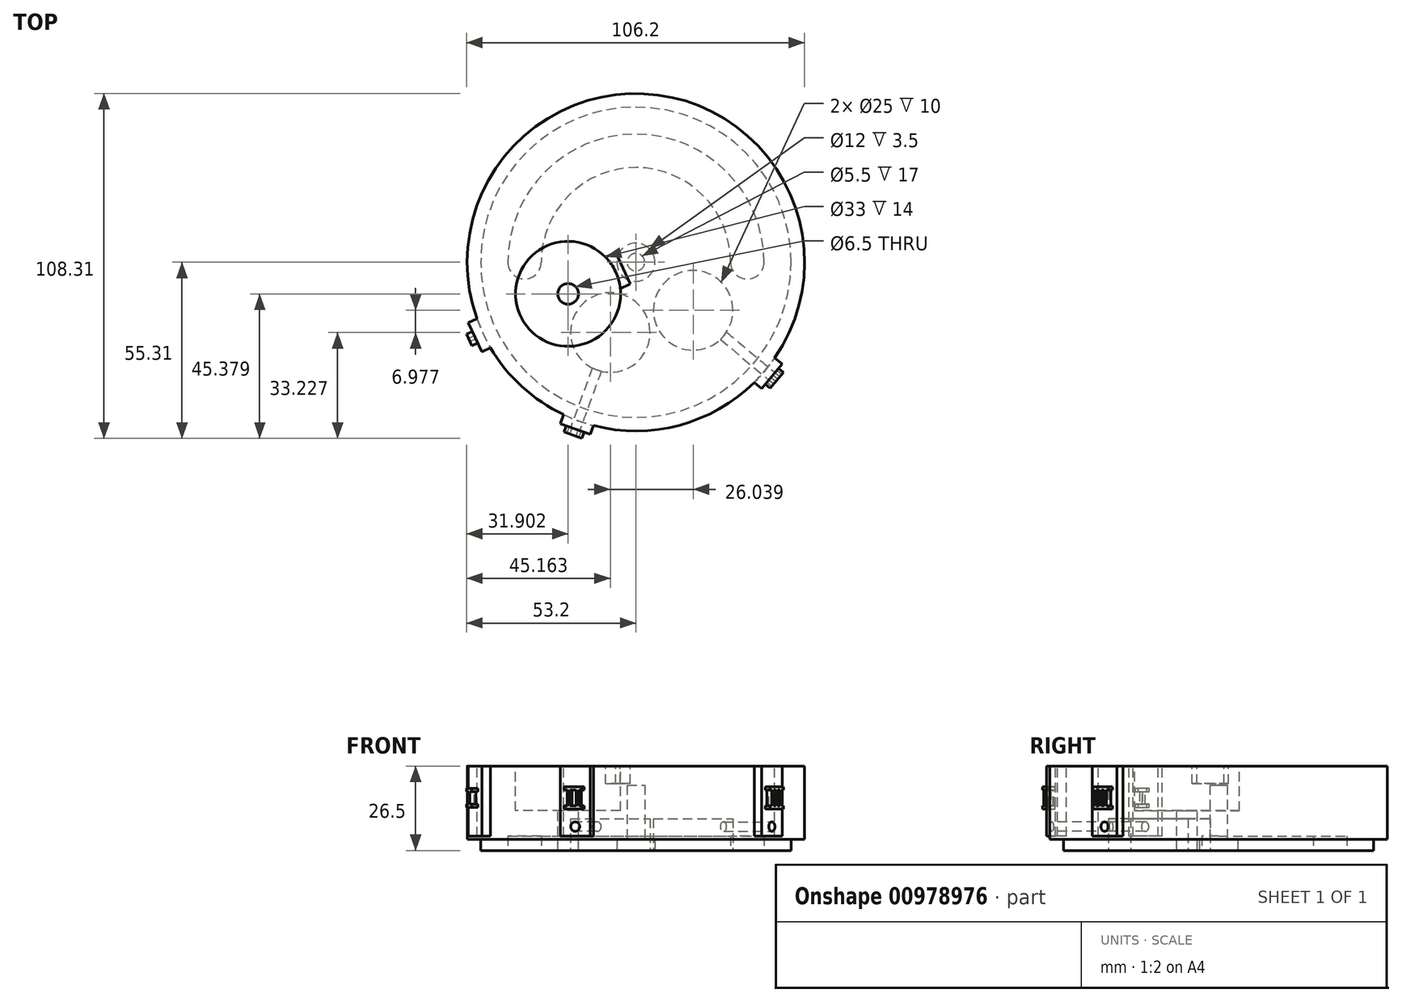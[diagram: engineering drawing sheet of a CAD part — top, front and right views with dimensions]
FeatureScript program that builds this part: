
annotation { "Feature Type Name" : "Feature", "Feature Type Description" : "" }
export const myFeature = defineFeature(function(context is Context, id is Id, definition is map)
    precondition{}
    {
        {
            var Q0;
            Q0=qCreatedBy(makeId("Top.planeOp"),FACE);
            var sketch = newSketch(context, id + "F0", { "sketchPlane" : qUnion([Q0])});
            skCircle(sketch, "E0", {"center": v(0, 0) * mm, "radius": 53 * mm});
            skSolve(sketch);
        }
        {
            var Q0;
            Q0=makeQuery(id+"F0.imprint","IMPRINT",FACE,{"disambiguationData":[TD([[makeQuery(id+"F0.imprint","IMPRINT",EDGE,{"derivedFrom":sQuery(id+"F0.wireOp",EDGE,"E0")}),1.0]])]});
            extrude(context, id + "F1", {"entities" : qUnion([Q0]), "depth" : 26.5 * mm, "offsetDistance" : 25 * mm});
        }
        {
            var Q0;
            Q0=makeQuery(id+"F1.opExtrude","CAP_FACE",FACE,{"disambiguationData":[OSD([sQuery(id+"F0.wireOp",EDGE,"E0")])],"isStart":true});
            var sketch = newSketch(context, id + "F2", { "sketchPlane" : qUnion([Q0])});
            skCircle(sketch, "E1", {"center": v(0, 0) * mm, "radius": 6 * mm});
            skCircle(sketch, "E2", {"center": v(0, 0) * mm, "radius": 48.75 * mm});
            skCircle(sketch, "E3", {"center": v(-35, 0) * mm, "radius": 5.25 * mm});
            skCircle(sketch, "E4", {"center": v(35, 0) * mm, "radius": 5.25 * mm});
            skCircle(sketch, "E5", {"center": v(0, 0) * mm, "radius": 29.75 * mm});
            skCircle(sketch, "E6", {"center": v(0, 0) * mm, "radius": 40.25 * mm});
            skCircle(sketch, "E7", {"center": v(-8.04, 22.08) * mm, "radius": 12.5 * mm});
            skCircle(sketch, "E8", {"center": v(18, 15.1) * mm, "radius": 12.5 * mm});
            skLineSegment(sketch, "E9", {"start": v(18, 15.1) * mm, "end": v(0, 0) * mm});
            skLineSegment(sketch, "E10", {"start": v(0, 0) * mm, "end": v(0, 10.25) * mm});
            skSolve(sketch);
        }
        {
            var Q0;
            Q0=makeQuery(id+"F2.imprint","IMPRINT",FACE,{"disambiguationData":[TD([[makeQuery(id+"F2.imprint","IMPRINT",EDGE,{"derivedFrom":sQuery(id+"F2.wireOp",EDGE,"E1")}),1.0]])]});
            var Q1;
            Q1=makeQuery(id+"F2.imprint","IMPRINT",FACE,{"disambiguationData":[TD([[makeQuery(id+"F2.imprint","IMPRINT",EDGE,{"derivedFrom":sQuery(id+"F2.wireOp",EDGE,"E2")}),-1.0]])]});
            extrude(context, id + "F3", {"entities" : qUnion([Q0, Q1]), "operationType" : NewBodyOperationType.REMOVE, "oppositeDirection" : true, "depth" : 3.5 * mm, "offsetDistance" : 25 * mm});
        }
        {
            var Q0;
            Q0=makeQuery(id+"F3.boolean.opBoolean","COPY",FACE,{"derivedFrom":makeQuery(id+"F3.opExtrude","CAP_FACE",FACE,{"disambiguationData":[OSD([sQuery(id+"F2.wireOp",EDGE,"E1")])],"isStart":false})});
            var sketch = newSketch(context, id + "F4", { "sketchPlane" : qUnion([Q0])});
            skCircle(sketch, "E11", {"center": v(0, 0) * mm, "radius": 2.75 * mm});
            skSolve(sketch);
        }
        {
            var Q0;
            Q0=makeQuery(id+"F4.imprint","IMPRINT",FACE,{"disambiguationData":[TD([[makeQuery(id+"F4.imprint","IMPRINT",EDGE,{"derivedFrom":sQuery(id+"F4.wireOp",EDGE,"E11")}),1.0]])]});
            extrude(context, id + "F5", {"entities" : qUnion([Q0]), "operationType" : NewBodyOperationType.REMOVE, "oppositeDirection" : true, "depth" : 17 * mm, "offsetDistance" : 25 * mm});
        }
        {
            var Q0;
            {var subQ0=sQuery(id+"F2.wireOp",EDGE,"E3");var subQ1=makeQuery(id+"F2.imprint","INTERSECT",VERTEX,{"derivedFrom":[subQ0,sQuery(id+"F2.wireOp",EDGE,"E5")]});Q0=makeQuery(id+"F2.imprint","IMPRINT",FACE,{"disambiguationData":[TD([[makeQuery(id+"F2.imprint","IMPRINT",EDGE,{"disambiguationData":[TD([[subQ1,-1.0]])],"derivedFrom":subQ0}),1.0]])]});}
            var Q1;
            {var subQ0=sQuery(id+"F2.wireOp",EDGE,"E5");var subQ1=sQuery(id+"F2.wireOp",EDGE,"E3");var subQ2=makeQuery(id+"F2.imprint","INTERSECT",VERTEX,{"derivedFrom":[subQ1,subQ0]});Q1=makeQuery(id+"F2.imprint","IMPRINT",FACE,{"disambiguationData":[TD([[makeQuery(id+"F2.imprint","IMPRINT",EDGE,{"disambiguationData":[TD([[subQ2,1.0]])],"derivedFrom":subQ1}),-1.0]])]});}
            var Q2;
            {var subQ0=sQuery(id+"F2.wireOp",EDGE,"E4");var subQ1=makeQuery(id+"F2.imprint","INTERSECT",VERTEX,{"derivedFrom":[subQ0,sQuery(id+"F2.wireOp",EDGE,"E5")]});Q2=makeQuery(id+"F2.imprint","IMPRINT",FACE,{"disambiguationData":[TD([[makeQuery(id+"F2.imprint","IMPRINT",EDGE,{"disambiguationData":[TD([[subQ1,1.0]])],"derivedFrom":subQ0}),1.0]])]});}
            extrude(context, id + "F6", {"entities" : qUnion([Q0, Q1, Q2]), "operationType" : NewBodyOperationType.REMOVE, "oppositeDirection" : true, "depth" : 4.5 * mm, "offsetDistance" : 25 * mm});
        }
        {
            var Q0;
            Q0=makeQuery(id+"F1.opExtrude","CAP_FACE",FACE,{"disambiguationData":[OSD([sQuery(id+"F0.wireOp",EDGE,"E0")])],"isStart":false});
            var sketch = newSketch(context, id + "F7", { "sketchPlane" : qUnion([Q0])});
            skCircle(sketch, "E12", {"center": v(-21.3, -9.93) * mm, "radius": 16.5 * mm});
            skLineSegment(sketch, "E13", {"start": v(-21.3, -9.93) * mm, "end": v(0, 0) * mm});
            skLineSegment(sketch, "E14", {"start": v(0, 0) * mm, "end": v(0, -53) * mm});
            skLineSegment(sketch, "E15", {"start": v(-49.93, -17.77) * mm, "end": v(-52.65, -19.04) * mm});
            skLineSegment(sketch, "E16", {"start": v(-52.65, -19.04) * mm, "end": v(-48.43, -28.1) * mm});
            skLineSegment(sketch, "E17", {"start": v(-48.43, -28.1) * mm, "end": v(-45.7, -26.83) * mm});
            skLineSegment(sketch, "E18", {"start": v(0, 0) * mm, "end": v(-18.13, -49.8) * mm});
            skLineSegment(sketch, "E19", {"start": v(0, 0) * mm, "end": v(40.6, -34.07) * mm});
            skLineSegment(sketch, "E20", {"start": v(-22.74, -47.87) * mm, "end": v(-23.77, -50.7) * mm});
            skLineSegment(sketch, "E21", {"start": v(-23.77, -50.7) * mm, "end": v(-14.37, -54.11) * mm});
            skLineSegment(sketch, "E22", {"start": v(-14.37, -54.11) * mm, "end": v(-13.35, -51.3) * mm});
            skLineSegment(sketch, "E23", {"start": v(43.63, -30.09) * mm, "end": v(45.93, -32.01) * mm});
            skLineSegment(sketch, "E24", {"start": v(45.93, -32.01) * mm, "end": v(39.5, -39.67) * mm});
            skLineSegment(sketch, "E25", {"start": v(39.5, -39.67) * mm, "end": v(37.2, -37.75) * mm});
            skLineSegment(sketch, "E26", {"start": v(-9.52, 1.63) * mm, "end": v(-6.35, 3.1) * mm});
            skLineSegment(sketch, "E27", {"start": v(-6.35, 3.1) * mm, "end": v(-1.7, -6.86) * mm});
            skLineSegment(sketch, "E28", {"start": v(-1.7, -6.86) * mm, "end": v(-4.87, -8.34) * mm});
            skSolve(sketch);
        }
        {
            var Q0;
            Q0=makeQuery(id+"F7.imprint","IMPRINT",FACE,{"disambiguationData":[TD([[makeQuery(id+"F7.imprint","IMPRINT",EDGE,{"derivedFrom":sQuery(id+"F7.wireOp",EDGE,"E12")}),1.0]])]});
            extrude(context, id + "F8", {"entities" : qUnion([Q0]), "operationType" : NewBodyOperationType.REMOVE, "oppositeDirection" : true, "depth" : 14 * mm, "offsetDistance" : 25 * mm});
        }
        {
            var Q0;
            Q0=makeQuery(id+"F8.boolean.opBoolean","COPY",FACE,{"derivedFrom":makeQuery(id+"F8.opExtrude","CAP_FACE",FACE,{"disambiguationData":[OSD([sQuery(id+"F7.wireOp",EDGE,"E12")])],"isStart":false})});
            var sketch = newSketch(context, id + "F9", { "sketchPlane" : qUnion([Q0])});
            skCircle(sketch, "E29", {"center": v(-21.3, -9.93) * mm, "radius": 3.25 * mm});
            skSolve(sketch);
        }
        {
            var Q0;
            Q0=makeQuery(id+"F9.imprint","IMPRINT",FACE,{"disambiguationData":[TD([[makeQuery(id+"F9.imprint","IMPRINT",EDGE,{"derivedFrom":sQuery(id+"F9.wireOp",EDGE,"E29")}),1.0]])]});
            extrude(context, id + "F10", {"entities" : qUnion([Q0]), "operationType" : NewBodyOperationType.REMOVE, "oppositeDirection" : true, "depth" : 12.5 * mm, "offsetDistance" : 25 * mm});
        }
        {
            var Q0;
            {var subQ0=sQuery(id+"F2.wireOp",EDGE,"E7");var subQ1=sQuery(id+"F2.wireOp",EDGE,"E5");var subQ2=makeQuery(id+"F2.imprint","INTERSECT",VERTEX,{"disambiguationData":[OD(0.0)],"derivedFrom":[subQ1,subQ0]});Q0=makeQuery(id+"F2.imprint","IMPRINT",FACE,{"disambiguationData":[TD([[makeQuery(id+"F2.imprint","IMPRINT",EDGE,{"disambiguationData":[TD([[subQ2,-1.0]])],"derivedFrom":subQ1}),1.0]])]});}
            var Q1;
            {var subQ0=sQuery(id+"F2.wireOp",EDGE,"E7");var subQ1=sQuery(id+"F2.wireOp",EDGE,"E5");var subQ2=makeQuery(id+"F2.imprint","INTERSECT",VERTEX,{"disambiguationData":[OD(0.0)],"derivedFrom":[subQ1,subQ0]});Q1=makeQuery(id+"F2.imprint","IMPRINT",FACE,{"disambiguationData":[TD([[makeQuery(id+"F2.imprint","IMPRINT",EDGE,{"disambiguationData":[TD([[subQ2,-1.0]])],"derivedFrom":subQ1}),-1.0]])]});}
            var Q2;
            {var subQ0=sQuery(id+"F2.wireOp",EDGE,"E8");var subQ1=sQuery(id+"F2.wireOp",EDGE,"E5");var subQ2=makeQuery(id+"F2.imprint","INTERSECT",VERTEX,{"disambiguationData":[OD(0.0)],"derivedFrom":[subQ1,subQ0]});Q2=makeQuery(id+"F2.imprint","IMPRINT",FACE,{"disambiguationData":[TD([[makeQuery(id+"F2.imprint","IMPRINT",EDGE,{"disambiguationData":[TD([[subQ2,-1.0]])],"derivedFrom":subQ1}),1.0]])]});}
            var Q3;
            {var subQ0=sQuery(id+"F2.wireOp",EDGE,"E8");var subQ1=sQuery(id+"F2.wireOp",EDGE,"E5");var subQ2=makeQuery(id+"F2.imprint","INTERSECT",VERTEX,{"disambiguationData":[OD(0.0)],"derivedFrom":[subQ1,subQ0]});Q3=makeQuery(id+"F2.imprint","IMPRINT",FACE,{"disambiguationData":[TD([[makeQuery(id+"F2.imprint","IMPRINT",EDGE,{"disambiguationData":[TD([[subQ2,-1.0]])],"derivedFrom":subQ1}),-1.0]])]});}
            extrude(context, id + "F11", {"entities" : qUnion([Q0, Q1, Q2, Q3]), "operationType" : NewBodyOperationType.REMOVE, "oppositeDirection" : true, "depth" : 10 * mm, "offsetDistance" : 25 * mm});
        }
        {
            var Q0;
            {var subQ0=sQuery(id+"F7.wireOp",EDGE,"E15");Q0=makeQuery(id+"F7.imprint","IMPRINT",FACE,{"disambiguationData":[TD([[makeQuery(id+"F7.imprint","IMPRINT",EDGE,{"derivedFrom":subQ0}),1.0]])]});}
            var Q1;
            {var subQ3=sQuery(id+"F7.wireOp",EDGE,"E20");Q1=makeQuery(id+"F7.imprint","IMPRINT",FACE,{"disambiguationData":[TD([[makeQuery(id+"F7.imprint","IMPRINT",EDGE,{"derivedFrom":subQ3}),1.0]])]});}
            var Q2;
            {var subQ3=sQuery(id+"F7.wireOp",EDGE,"E23");Q2=makeQuery(id+"F7.imprint","IMPRINT",FACE,{"disambiguationData":[TD([[makeQuery(id+"F7.imprint","IMPRINT",EDGE,{"derivedFrom":subQ3}),-1.0]])]});}
            extrude(context, id + "F12", {"entities" : qUnion([Q0, Q1, Q2]), "operationType" : NewBodyOperationType.ADD, "oppositeDirection" : true, "depth" : 22 * mm, "offsetDistance" : 25 * mm});
        }
        {
            var Q0;
            {var subQ0=sQuery(id+"F7.wireOp",EDGE,"E26");Q0=makeQuery(id+"F7.imprint","IMPRINT",FACE,{"disambiguationData":[TD([[makeQuery(id+"F7.imprint","IMPRINT",EDGE,{"derivedFrom":subQ0}),-1.0]])]});}
            var Q1;
            {var subQ5=sQuery(id+"F7.wireOp",EDGE,"E28");var subQ7=sQuery(id+"F7.wireOp",EDGE,"E12");var subQ9=makeQuery(id+"F7.imprint","INTERSECT",VERTEX,{"derivedFrom":[subQ7,subQ5]});Q1=makeQuery(id+"F7.imprint","IMPRINT",FACE,{"disambiguationData":[TD([[makeQuery(id+"F7.imprint","IMPRINT",EDGE,{"disambiguationData":[TD([[subQ9,-1.0]])],"derivedFrom":subQ7}),-1.0]])]});}
            var Q2;
            {var subQ0=sQuery(id+"F7.wireOp",EDGE,"E27");var subQ1=sQuery(id+"F7.wireOp",EDGE,"E18");var subQ2=makeQuery(id+"F7.imprint","INTERSECT",VERTEX,{"derivedFrom":[subQ1,subQ0]});Q2=makeQuery(id+"F7.imprint","IMPRINT",FACE,{"disambiguationData":[TD([[makeQuery(id+"F7.imprint","IMPRINT",EDGE,{"disambiguationData":[TD([[subQ2,-1.0]])],"derivedFrom":subQ1}),1.0]])]});}
            extrude(context, id + "F13", {"entities" : qUnion([Q0, Q1, Q2]), "operationType" : NewBodyOperationType.REMOVE, "oppositeDirection" : true, "depth" : 5.5 * mm, "offsetDistance" : 25 * mm});
        }
        {
            var Q0;
            Q0=makeQuery(id+"F12.opExtrude","SWEPT_FACE",FACE,{"disambiguationData":[OSD([sQuery(id+"F7.wireOp",EDGE,"E21")])]});
            var sketch = newSketch(context, id + "F14", { "sketchPlane" : qUnion([Q0])});
            skCircle(sketch, "E30", {"center": v(0, 7.5) * mm, "radius": 1.5 * mm});
            skLineSegment(sketch, "E31", {"start": v(-3, 20) * mm, "end": v(3, 20) * mm});
            skLineSegment(sketch, "E32", {"start": v(3, 20) * mm, "end": v(3, 19) * mm});
            skLineSegment(sketch, "E33", {"start": v(3, 19) * mm, "end": v(2, 19) * mm});
            skLineSegment(sketch, "E34", {"start": v(2, 19) * mm, "end": v(2, 14) * mm});
            skLineSegment(sketch, "E35", {"start": v(2, 14) * mm, "end": v(3, 14) * mm});
            skLineSegment(sketch, "E36", {"start": v(3, 14) * mm, "end": v(3, 13) * mm});
            skLineSegment(sketch, "E37", {"start": v(3, 13) * mm, "end": v(-3, 13) * mm});
            skLineSegment(sketch, "E38", {"start": v(-3, 13) * mm, "end": v(-3, 14) * mm});
            skLineSegment(sketch, "E39", {"start": v(-3, 14) * mm, "end": v(-2, 14) * mm});
            skLineSegment(sketch, "E40", {"start": v(-2, 14) * mm, "end": v(-2, 19) * mm});
            skLineSegment(sketch, "E41", {"start": v(-2, 19) * mm, "end": v(-3, 19) * mm});
            skLineSegment(sketch, "E42", {"start": v(-3, 19) * mm, "end": v(-3, 20) * mm});
            skLineSegment(sketch, "E43", {"start": v(-1, 19) * mm, "end": v(1, 19) * mm});
            skLineSegment(sketch, "E44", {"start": v(1, 19) * mm, "end": v(1, 14) * mm});
            skLineSegment(sketch, "E45", {"start": v(1, 14) * mm, "end": v(-1, 14) * mm});
            skLineSegment(sketch, "E46", {"start": v(-1, 14) * mm, "end": v(-1, 19) * mm});
            skSolve(sketch);
        }
        {
            var Q0;
            Q0=makeQuery(id+"F14.imprint","IMPRINT",FACE,{"disambiguationData":[TD([[makeQuery(id+"F14.imprint","IMPRINT",EDGE,{"derivedFrom":sQuery(id+"F14.wireOp",EDGE,"E30")}),1.0]])]});
            extrude(context, id + "F15", {"entities" : qUnion([Q0]), "operationType" : NewBodyOperationType.REMOVE, "oppositeDirection" : true, "depth" : 25 * mm, "offsetDistance" : 25 * mm});
        }
        {
            var Q0;
            Q0=makeQuery(id+"F12.opExtrude","SWEPT_FACE",FACE,{"disambiguationData":[OSD([sQuery(id+"F7.wireOp",EDGE,"E24")])]});
            var sketch = newSketch(context, id + "F16", { "sketchPlane" : qUnion([Q0])});
            skCircle(sketch, "E47", {"center": v(0, 7.5) * mm, "radius": 1.5 * mm});
            skLineSegment(sketch, "E48", {"start": v(-3.25, 20) * mm, "end": v(3.25, 20) * mm});
            skLineSegment(sketch, "E49", {"start": v(3.25, 20) * mm, "end": v(3.25, 19) * mm});
            skLineSegment(sketch, "E50", {"start": v(3.25, 19) * mm, "end": v(2.5, 19) * mm});
            skLineSegment(sketch, "E51", {"start": v(2.5, 19) * mm, "end": v(2.5, 14) * mm});
            skLineSegment(sketch, "E52", {"start": v(2.5, 14) * mm, "end": v(3.25, 14) * mm});
            skLineSegment(sketch, "E53", {"start": v(3.25, 14) * mm, "end": v(3.25, 13) * mm});
            skLineSegment(sketch, "E54", {"start": v(3.25, 13) * mm, "end": v(-3.25, 13) * mm});
            skLineSegment(sketch, "E55", {"start": v(-3.25, 13) * mm, "end": v(-3.25, 14) * mm});
            skLineSegment(sketch, "E56", {"start": v(-3.25, 14) * mm, "end": v(-2.5, 14) * mm});
            skLineSegment(sketch, "E57", {"start": v(-2.5, 14) * mm, "end": v(-2.5, 19) * mm});
            skLineSegment(sketch, "E58", {"start": v(-2.5, 19) * mm, "end": v(-3.25, 19) * mm});
            skLineSegment(sketch, "E59", {"start": v(-3.25, 19) * mm, "end": v(-3.25, 20) * mm});
            skLineSegment(sketch, "E60", {"start": v(-1.5, 14) * mm, "end": v(-1.5, 19) * mm});
            skLineSegment(sketch, "E61", {"start": v(-1.5, 19) * mm, "end": v(-0.5, 19) * mm});
            skLineSegment(sketch, "E62", {"start": v(-0.5, 19) * mm, "end": v(-0.5, 14) * mm});
            skLineSegment(sketch, "E63", {"start": v(-0.5, 14) * mm, "end": v(-1.5, 14) * mm});
            skLineSegment(sketch, "E64", {"start": v(0.5, 14) * mm, "end": v(0.5, 19) * mm});
            skLineSegment(sketch, "E65", {"start": v(0.5, 19) * mm, "end": v(1.5, 19) * mm});
            skLineSegment(sketch, "E66", {"start": v(1.5, 19) * mm, "end": v(1.5, 14) * mm});
            skLineSegment(sketch, "E67", {"start": v(1.5, 14) * mm, "end": v(0.5, 14) * mm});
            skSolve(sketch);
        }
        {
            var Q0;
            Q0=makeQuery(id+"F16.imprint","IMPRINT",FACE,{"disambiguationData":[TD([[makeQuery(id+"F16.imprint","IMPRINT",EDGE,{"derivedFrom":sQuery(id+"F16.wireOp",EDGE,"E47")}),1.0]])]});
            extrude(context, id + "F17", {"entities" : qUnion([Q0]), "operationType" : NewBodyOperationType.REMOVE, "oppositeDirection" : true, "depth" : 25 * mm, "offsetDistance" : 25 * mm});
        }
        {
            var Q0;
            Q0=makeQuery(id+"F12.opExtrude","SWEPT_FACE",FACE,{"disambiguationData":[OSD([sQuery(id+"F7.wireOp",EDGE,"E16")])]});
            var sketch = newSketch(context, id + "F18", { "sketchPlane" : qUnion([Q0])});
            skLineSegment(sketch, "E68", {"start": v(-2, 19.5) * mm, "end": v(2, 19.5) * mm});
            skLineSegment(sketch, "E69", {"start": v(2, 19.5) * mm, "end": v(2, 18.5) * mm});
            skLineSegment(sketch, "E70", {"start": v(2, 18.5) * mm, "end": v(0.5, 18.5) * mm});
            skLineSegment(sketch, "E71", {"start": v(0.5, 18.5) * mm, "end": v(0.5, 14.5) * mm});
            skLineSegment(sketch, "E72", {"start": v(0.5, 14.5) * mm, "end": v(2, 14.5) * mm});
            skLineSegment(sketch, "E73", {"start": v(2, 14.5) * mm, "end": v(2, 13.5) * mm});
            skLineSegment(sketch, "E74", {"start": v(2, 13.5) * mm, "end": v(-2, 13.5) * mm});
            skLineSegment(sketch, "E75", {"start": v(-2, 13.5) * mm, "end": v(-2, 14.5) * mm});
            skLineSegment(sketch, "E76", {"start": v(-2, 14.5) * mm, "end": v(-0.5, 14.5) * mm});
            skLineSegment(sketch, "E77", {"start": v(-0.5, 14.5) * mm, "end": v(-0.5, 18.5) * mm});
            skLineSegment(sketch, "E78", {"start": v(-0.5, 18.5) * mm, "end": v(-2, 18.5) * mm});
            skLineSegment(sketch, "E79", {"start": v(-2, 18.5) * mm, "end": v(-2, 19.5) * mm});
            skSolve(sketch);
        }
        {
            var Q0;
            Q0=makeQuery(id+"F18.imprint","IMPRINT",FACE,{"disambiguationData":[TD([[makeQuery(id+"F18.imprint","IMPRINT",EDGE,{"derivedFrom":sQuery(id+"F18.wireOp",EDGE,"E68")}),-1.0]])]});
            extrude(context, id + "F19", {"entities" : qUnion([Q0]), "operationType" : NewBodyOperationType.ADD, "depth" : 2 * mm, "offsetDistance" : 25 * mm});
        }
        {
            var Q0;
            Q0=makeQuery(id+"F14.imprint","IMPRINT",FACE,{"disambiguationData":[TD([[makeQuery(id+"F14.imprint","IMPRINT",EDGE,{"derivedFrom":sQuery(id+"F14.wireOp",EDGE,"E31")}),-1.0]])]});
            extrude(context, id + "F20", {"entities" : qUnion([Q0]), "operationType" : NewBodyOperationType.ADD, "depth" : 2 * mm, "offsetDistance" : 25 * mm});
        }
        {
            var Q0;
            Q0=makeQuery(id+"F16.imprint","IMPRINT",FACE,{"disambiguationData":[TD([[makeQuery(id+"F16.imprint","IMPRINT",EDGE,{"derivedFrom":sQuery(id+"F16.wireOp",EDGE,"E48")}),-1.0]])]});
            extrude(context, id + "F21", {"entities" : qUnion([Q0]), "operationType" : NewBodyOperationType.ADD, "depth" : 2 * mm, "offsetDistance" : 25 * mm});
        }
    });
